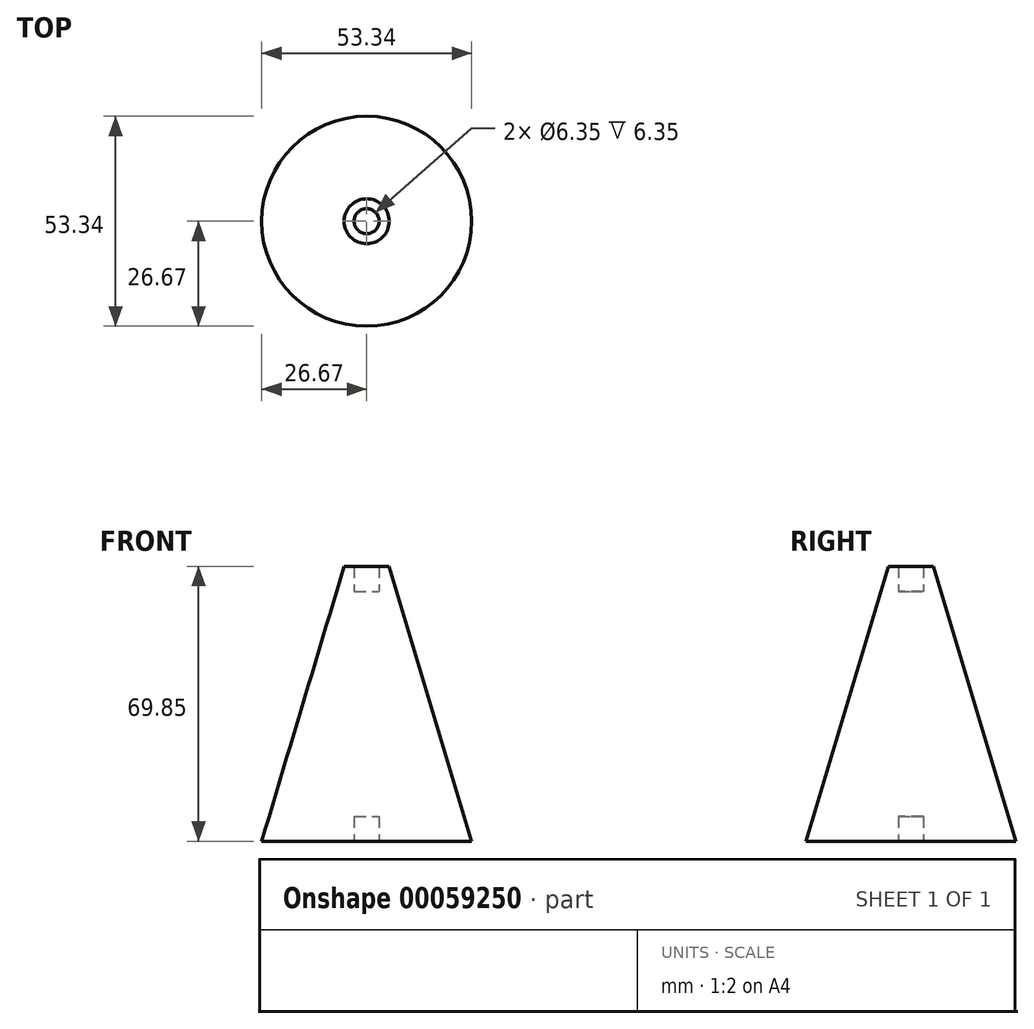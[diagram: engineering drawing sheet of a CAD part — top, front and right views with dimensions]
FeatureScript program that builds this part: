
annotation { "Feature Type Name" : "Feature", "Feature Type Description" : "" }
export const myFeature = defineFeature(function(context is Context, id is Id, definition is map)
    precondition{}
    {
        {
            var Q0;
            Q0=qCreatedBy(makeId("Front.planeOp"),FACE);
            var sketch = newSketch(context, id + "F0", { "sketchPlane" : qUnion([Q0])});
            skLineSegment(sketch, "E0", {"start": v(5.72, 48.07) * mm, "end": v(26.67, -21.78) * mm});
            skLineSegment(sketch, "E1", {"start": v(26.67, -21.78) * mm, "end": v(0, -21.78) * mm});
            skLineSegment(sketch, "E2", {"start": v(0, -21.78) * mm, "end": v(0, 41.72) * mm});
            skLineSegment(sketch, "E3", {"start": v(0, 41.72) * mm, "end": v(3.17, 41.72) * mm});
            skLineSegment(sketch, "E4", {"start": v(3.18, 41.72) * mm, "end": v(3.18, 48.07) * mm});
            skLineSegment(sketch, "E5", {"start": v(3.17, 48.07) * mm, "end": v(5.71, 48.07) * mm});
            skPoint(sketch, "E6.orphan", {"position": v(0, 67.12) * mm});
            skSolve(sketch);
        }
        {
            var Q0;
            Q0 = qSketchRegion(id + "F0", true);
            var Q1;
            Q1=sQuery(id+"F0.wireOp",EDGE,"E2");
            revolve(context, id + "F1", {"entities" : qUnion([Q0]), "axis" : qUnion([Q1]), "revolveType" : RevolveType.FULL});
        }
        {
            var Q0;
            Q0=makeQuery(id+"F1.opRevolve","SWEPT_FACE",FACE,{"disambiguationData":[OSD([sQuery(id+"F0.wireOp",EDGE,"E1")])]});
            var sketch = newSketch(context, id + "F2", { "sketchPlane" : qUnion([Q0])});
            skCircle(sketch, "E7", {"center": v(0, 0) * mm, "radius": 3.18 * mm});
            skSolve(sketch);
        }
        {
            var Q0;
            Q0 = qSketchRegion(id + "F2", true);
            extrude(context, id + "F3", {"entities" : qUnion([Q0]), "operationType" : NewBodyOperationType.REMOVE, "oppositeDirection" : true, "depth" : 6.35 * mm});
        }
    });
